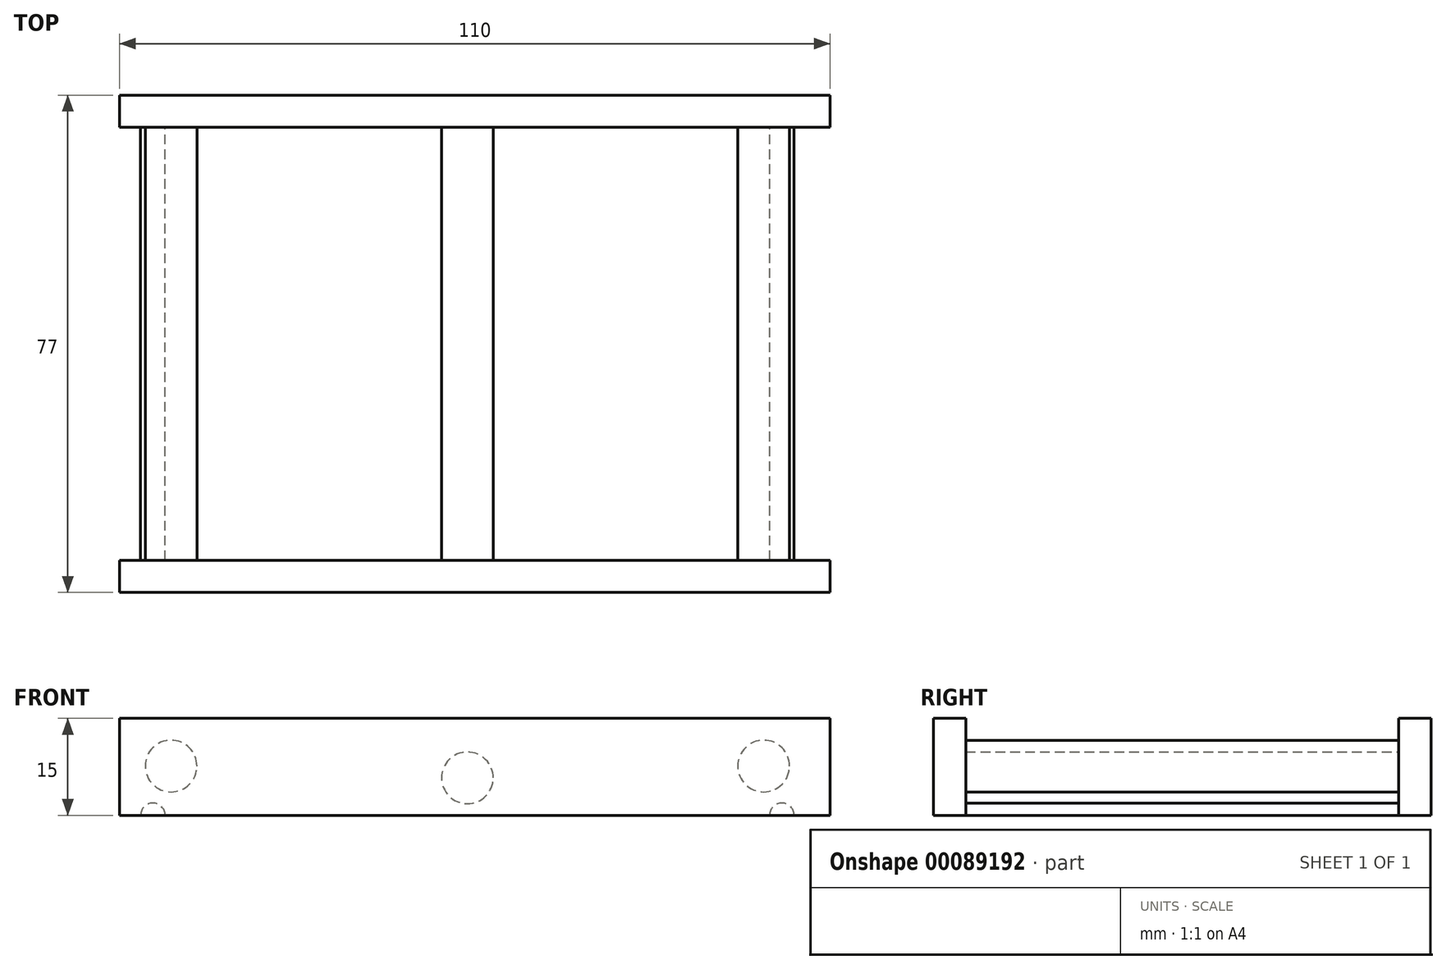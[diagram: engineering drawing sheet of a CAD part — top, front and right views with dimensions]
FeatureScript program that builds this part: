
annotation { "Feature Type Name" : "Feature", "Feature Type Description" : "" }
export const myFeature = defineFeature(function(context is Context, id is Id, definition is map)
    precondition{}
    {
        {
            var Q0;
            Q0=qCreatedBy(makeId("Front.planeOp"),FACE);
            var sketch = newSketch(context, id + "F0", { "sketchPlane" : qUnion([Q0])});
            skLineSegment(sketch, "E0.bottom", {"start": v(-53.86, 12.06) * mm, "end": v(56.14, 12.06) * mm});
            skLineSegment(sketch, "E0.top", {"start": v(-53.86, -2.94) * mm, "end": v(56.14, -2.94) * mm});
            skLineSegment(sketch, "E0.left", {"start": v(-53.86, 12.06) * mm, "end": v(-53.86, -2.94) * mm});
            skLineSegment(sketch, "E0.right", {"start": v(56.14, 12.06) * mm, "end": v(56.14, -2.94) * mm});
            skSolve(sketch);
        }
        {
            var Q0;
            Q0=makeQuery(id+"F0.imprint","IMPRINT",FACE,{"disambiguationData":[TD([[makeQuery(id+"F0.imprint","IMPRINT",EDGE,{"derivedFrom":sQuery(id+"F0.wireOp",EDGE,"E0.bottom")}),-1.0]])]});
            extrude(context, id + "F1", {"entities" : qUnion([Q0]), "depth" : 5 * mm});
        }
        {
            var Q0;
            Q0=makeQuery(id+"F1.opExtrude","CAP_FACE",FACE,{"disambiguationData":[OSD([sQuery(id+"F0.wireOp",EDGE,"E0.bottom"),sQuery(id+"F0.wireOp",EDGE,"E0.top"),sQuery(id+"F0.wireOp",EDGE,"E0.left"),sQuery(id+"F0.wireOp",EDGE,"E0.right")])],"isStart":false});
            var sketch = newSketch(context, id + "F2", { "sketchPlane" : qUnion([Q0])});
            skCircle(sketch, "E1", {"center": v(0, 2.86) * mm, "radius": 4 * mm});
            skArc(sketch, "E2", {"start": v(-46.78, -2.94) * mm, "mid": v(-48.68, -1.04) * mm, "end": v(-50.58, -2.94) * mm});
            skLineSegment(sketch, "E3", {"start": v(0, -1.14) * mm, "end": v(-56.95, -1.14) * mm, "construction": true});
            skCircle(sketch, "E4", {"center": v(-45.86, 4.69) * mm, "radius": 4 * mm});
            skCircle(sketch, "E5.MirrorC", {"center": v(45.86, 4.69) * mm, "radius": 4 * mm});
            skArc(sketch, "E6.MirrorC", {"start": v(46.78, -2.94) * mm, "mid": v(48.68, -1.04) * mm, "end": v(50.58, -2.94) * mm});
            skLineSegment(sketch, "E7", {"start": v(-48.68, -2.94) * mm, "end": v(-46.78, -2.94) * mm});
            skLineSegment(sketch, "E8", {"start": v(-46.78, -2.94) * mm, "end": v(-48.68, -2.94) * mm});
            skLineSegment(sketch, "E9", {"start": v(-48.68, -2.94) * mm, "end": v(-50.58, -2.94) * mm});
            skLineSegment(sketch, "E10", {"start": v(46.78, -2.94) * mm, "end": v(50.58, -2.94) * mm});
            skSolve(sketch);
        }
        {
            var Q0;
            Q0 = qSketchRegion(id + "F2", true);
            extrude(context, id + "F3", {"entities" : qUnion([Q0]), "operationType" : NewBodyOperationType.ADD, "depth" : 67 / 2 * mm});
        }
        {
            var Q0;
            Q0=makeQuery(id+"F1.opExtrude","SWEPT_BODY",BODY,{"disambiguationData":[OSD([sQuery(id+"F0.wireOp",EDGE,"E0.bottom"),sQuery(id+"F0.wireOp",EDGE,"E0.top"),sQuery(id+"F0.wireOp",EDGE,"E0.left"),sQuery(id+"F0.wireOp",EDGE,"E0.right")])]});
            var Q1;
            Q1=makeQuery(id+"F3.opExtrude","CAP_FACE",FACE,{"disambiguationData":[OSD([sQuery(id+"F2.wireOp",EDGE,"E4")])],"isStart":false});
            mirror(context, id + "F4", {"operationType" : NewBodyOperationType.ADD, "entities" : qUnion([Q0]), "mirrorPlane" : qUnion([Q1])});
        }
    });
